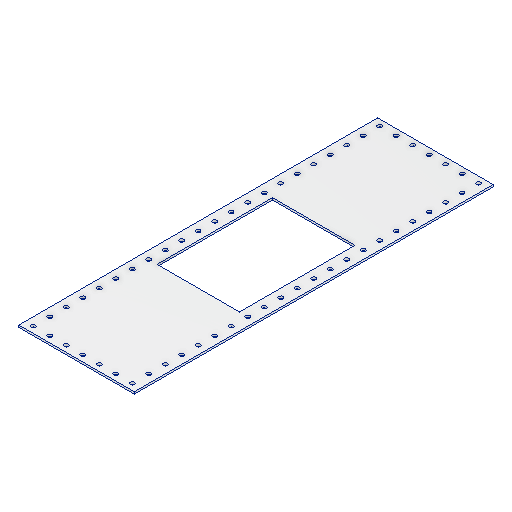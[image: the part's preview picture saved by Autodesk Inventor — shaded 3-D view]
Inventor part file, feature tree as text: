
AUTODESK INVENTOR PART (.ipt)
format: ipt  version: 2022 (Build 260153000, 153)  size: 273,408 bytes
history: native  units: in
note: dims shown in document units (in); Inventor stores cm internally (conversion verified against a paired STEP export)
features: other x6, sketch x5, pattern_linear x4, sheet_metal_op x1
ambient origin geometry x8: Origin, YZ Plane, XZ Plane, XY Plane, X Axis, Y Axis, Z Axis, Center Point
bodies: Solid1 (feature_tree)
feature tree (16):
  sheet_metal_op  "Face1"
  pattern_linear  "Rectangular Pattern1"  Spacing1=0.5in  [1 undecoded]
  pattern_linear  "Rectangular Pattern2"  Spacing1=0.125in  [1 undecoded]
  pattern_linear  "Rectangular Pattern3"  Spacing1=0.0in  [1 undecoded]
  pattern_linear  "Rectangular Pattern4"  Count1=22 Spacing1=1.0in
  sketch  "Sketch1"  dims[d0=22.0in]
  other  "Plate1"
  sketch  "Sketch2"  dims[d1=7.0in]
  sketch  "Sketch3"  dims[d2=0.125in]
  sketch  "Sketch4"  dims[d3=0.26in]
  sketch  "Sketch5"  dims[d4=0.5in d5=0.5in d6=0.125in d7=0.0in d8=8.6614in d10=1.0in d11=2.3622in d13=1.0in d14=0.26in d15=0.26in d16=0.5in d17=0.5in d18=0.125in d19=0.0in d20=8.6614in d22=1.0in d23=2.3622in d25=1.0in d27=5.0in d28=7.0in d29=0.125in d30=0.0in d31=7.0in d32=0.125in d33=7.0in d34=0.125in d35=0.125in d36=0.0in]
  other  "Cut1"
  other  "Cut2"
  other  "Cut3"
  other  "Cut4"
  other  "Definition1"
note: 3 required parameter values undecoded (feature->parameter linkage not recoverable at this tier; creation-order binding heuristic only, values carry confidence <= 0.55)
